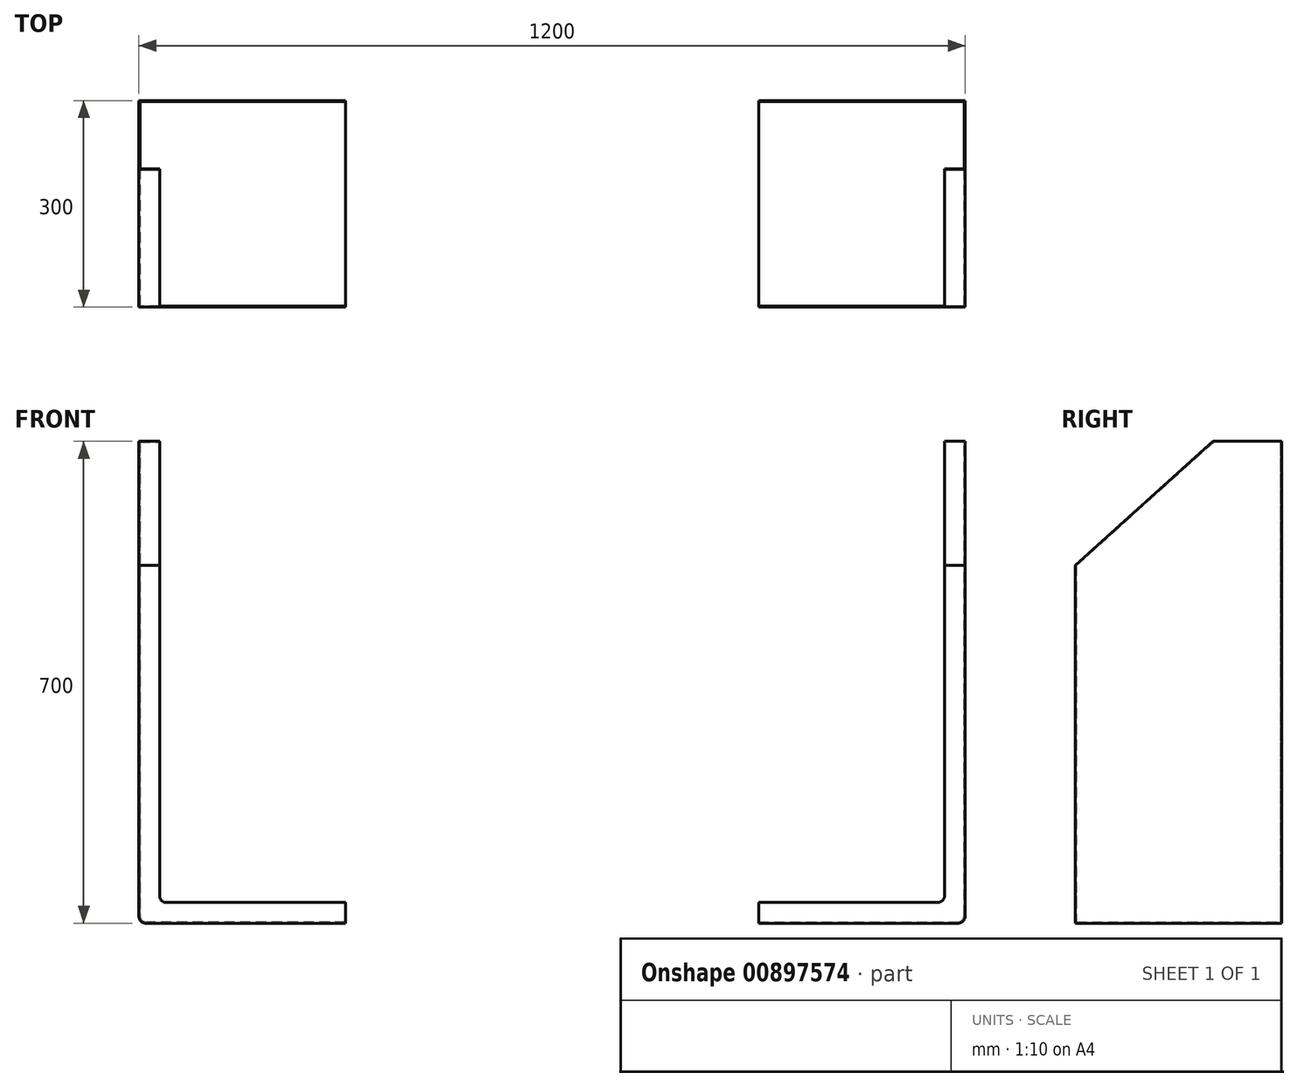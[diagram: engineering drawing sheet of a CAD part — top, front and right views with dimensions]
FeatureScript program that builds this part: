
annotation { "Feature Type Name" : "Feature", "Feature Type Description" : "" }
export const myFeature = defineFeature(function(context is Context, id is Id, definition is map)
    precondition{}
    {
        {
            var Q0;
            Q0=qCreatedBy(makeId("Front.planeOp"),FACE);
            var sketch = newSketch(context, id + "F0", { "sketchPlane" : qUnion([Q0])});
            skLineSegment(sketch, "E0.bottom", {"start": v(0, 0) * mm, "end": v(1.5, 0) * mm});
            skLineSegment(sketch, "E0.left", {"start": v(0, 0) * mm, "end": v(0, -690) * mm});
            skLineSegment(sketch, "E0.right", {"start": v(1.5, 0) * mm, "end": v(1.5, -688.5) * mm});
            skLineSegment(sketch, "E1.bottom", {"start": v(10, -700) * mm, "end": v(300, -700) * mm});
            skLineSegment(sketch, "E1.top", {"start": v(11.5, -698.5) * mm, "end": v(300, -698.5) * mm});
            skLineSegment(sketch, "E1.right", {"start": v(300, -700) * mm, "end": v(300, -698.5) * mm});
            skLineSegment(sketch, "E2", {"start": v(300, -700) * mm, "end": v(600, -700) * mm, "construction": true});
            skLineSegment(sketch, "E3", {"start": v(600, -700) * mm, "end": v(600, 159.83) * mm, "construction": true});
            skLineSegment(sketch, "E4.MirrorCS", {"start": v(1190, -700) * mm, "end": v(900, -700) * mm});
            skLineSegment(sketch, "E5.MirrorCS", {"start": v(1188.5, -698.5) * mm, "end": v(900, -698.5) * mm});
            skLineSegment(sketch, "E6.MirrorCS", {"start": v(900, -700) * mm, "end": v(900, -698.5) * mm});
            skLineSegment(sketch, "E7.MirrorCS", {"start": v(1200, 0) * mm, "end": v(1200, -690) * mm});
            skLineSegment(sketch, "E8.MirrorCS", {"start": v(1198.5, 0) * mm, "end": v(1198.5, -688.5) * mm});
            skLineSegment(sketch, "E9.MirrorCS", {"start": v(1200, 0) * mm, "end": v(1198.5, 0) * mm});
            skPoint(sketch, "E10.visualSharp", {"position": v(1.5, -698.5) * mm});
            skArc(sketch, "E10.filletArc", {"start": v(1.5, -688.5) * mm, "mid": v(4.43, -695.57) * mm, "end": v(11.5, -698.5) * mm});
            skPoint(sketch, "E11.visualSharp", {"position": v(0, -700) * mm});
            skArc(sketch, "E11.filletArc", {"start": v(0, -690) * mm, "mid": v(2.93, -697.07) * mm, "end": v(10, -700) * mm});
            skPoint(sketch, "E12.visualSharp", {"position": v(1198.5, -698.5) * mm});
            skArc(sketch, "E12.filletArc", {"start": v(1188.5, -698.5) * mm, "mid": v(1195.57, -695.57) * mm, "end": v(1198.5, -688.5) * mm});
            skPoint(sketch, "E13.visualSharp", {"position": v(1200, -700) * mm});
            skArc(sketch, "E13.filletArc", {"start": v(1190, -700) * mm, "mid": v(1197.07, -697.07) * mm, "end": v(1200, -690) * mm});
            skSolve(sketch);
        }
        {
            var Q0;
            Q0 = qSketchRegion(id + "F0", true);
            extrude(context, id + "F1", {"entities" : qUnion([Q0]), "depth" : 300 * mm, "offsetDistance" : 25 * mm});
        }
        {
            var Q0;
            Q0=makeQuery(id+"F1.opExtrude","CAP_EDGE",EDGE,{"disambiguationData":[OSD([sQuery(id+"F0.wireOp",EDGE,"E0.bottom")])],"isStart":false});
            chamfer(context, id + "F2", {"entities" : qUnion([Q0]), "chamferType" : ChamferType.TWO_OFFSETS, "width1" : 200 * mm, "oppositeDirection" : false, "width2" : 180 * mm});
        }
        {
            var Q0;
            Q0=makeQuery(id+"F1.opExtrude","CAP_FACE",FACE,{"disambiguationData":[OSD([sQuery(id+"F0.wireOp",EDGE,"E0.bottom"),sQuery(id+"F0.wireOp",EDGE,"E0.left"),sQuery(id+"F0.wireOp",EDGE,"E0.right"),sQuery(id+"F0.wireOp",EDGE,"E1.bottom"),sQuery(id+"F0.wireOp",EDGE,"E1.top"),sQuery(id+"F0.wireOp",EDGE,"E1.right")])],"isStart":false});
            var sketch = newSketch(context, id + "F3", { "sketchPlane" : qUnion([Q0])});
            skLineSegment(sketch, "E14.bottom", {"start": v(0, -180) * mm, "end": v(30, -180) * mm});
            skLineSegment(sketch, "E14.left", {"start": v(0, -180) * mm, "end": v(0, -690) * mm});
            skLineSegment(sketch, "E14.right", {"start": v(30, -180) * mm, "end": v(30, -660) * mm});
            skLineSegment(sketch, "E15.bottom", {"start": v(10, -700) * mm, "end": v(300, -700) * mm});
            skLineSegment(sketch, "E15.top", {"start": v(40, -670) * mm, "end": v(300, -670) * mm});
            skLineSegment(sketch, "E15.right", {"start": v(300, -700) * mm, "end": v(300, -670) * mm});
            skLineSegment(sketch, "E16.MirrorCS", {"start": v(900, -700) * mm, "end": v(900, -670) * mm});
            skLineSegment(sketch, "E17.MirrorCS", {"start": v(1160, -670) * mm, "end": v(900, -670) * mm});
            skLineSegment(sketch, "E18.MirrorCS", {"start": v(1190, -700) * mm, "end": v(900, -700) * mm});
            skLineSegment(sketch, "E19.MirrorCS", {"start": v(1170, -180) * mm, "end": v(1170, -660) * mm});
            skLineSegment(sketch, "E20.MirrorCS", {"start": v(1200, -180) * mm, "end": v(1200, -690) * mm});
            skLineSegment(sketch, "E21.MirrorCS", {"start": v(1200, -180) * mm, "end": v(1170, -180) * mm});
            skPoint(sketch, "E22.visualSharp", {"position": v(0, -700) * mm});
            skArc(sketch, "E22.filletArc", {"start": v(0, -690) * mm, "mid": v(2.93, -697.07) * mm, "end": v(10, -700) * mm});
            skPoint(sketch, "E23.visualSharp", {"position": v(30, -670) * mm});
            skArc(sketch, "E23.filletArc", {"start": v(30, -660) * mm, "mid": v(32.93, -667.07) * mm, "end": v(40, -670) * mm});
            skPoint(sketch, "E24.visualSharp", {"position": v(1170, -670) * mm});
            skArc(sketch, "E24.filletArc", {"start": v(1160, -670) * mm, "mid": v(1167.07, -667.07) * mm, "end": v(1170, -660) * mm});
            skPoint(sketch, "E25.visualSharp", {"position": v(1200, -700) * mm});
            skArc(sketch, "E25.filletArc", {"start": v(1190, -700) * mm, "mid": v(1197.07, -697.07) * mm, "end": v(1200, -690) * mm});
            skSolve(sketch);
        }
        {
            var Q0;
            Q0 = qSketchRegion(id + "F3", true);
            extrude(context, id + "F4", {"entities" : qUnion([Q0]), "operationType" : NewBodyOperationType.ADD, "oppositeDirection" : true, "depth" : 1.5 * mm, "offsetDistance" : 25 * mm});
        }
        {
            var Q0;
            Q0=makeQuery(id+"F2.opChamfer","BLEND_FACE",FACE,{"disambiguationData":[OSD([sQuery(id+"F0.wireOp",EDGE,"E0.bottom")])]});
            var sketch = newSketch(context, id + "F5", { "sketchPlane" : qUnion([Q0])});
            skLineSegment(sketch, "E26.bottom", {"start": v(0, -343.4) * mm, "end": v(30, -343.4) * mm});
            skLineSegment(sketch, "E26.top", {"start": v(0, -74.33) * mm, "end": v(30, -74.33) * mm});
            skLineSegment(sketch, "E26.left", {"start": v(0, -343.4) * mm, "end": v(0, -74.33) * mm});
            skLineSegment(sketch, "E26.right", {"start": v(30, -343.4) * mm, "end": v(30, -74.33) * mm});
            skLineSegment(sketch, "E27.MirrorCS", {"start": v(1170, -343.4) * mm, "end": v(1170, -74.33) * mm});
            skLineSegment(sketch, "E28.MirrorCS", {"start": v(1200, -343.4) * mm, "end": v(1170, -343.4) * mm});
            skLineSegment(sketch, "E29.MirrorCS", {"start": v(1200, -343.4) * mm, "end": v(1200, -74.33) * mm});
            skLineSegment(sketch, "E30.MirrorCS", {"start": v(1200, -74.33) * mm, "end": v(1170, -74.33) * mm});
            skSolve(sketch);
        }
        {
            var Q0;
            Q0 = qSketchRegion(id + "F5", true);
            extrude(context, id + "F6", {"entities" : qUnion([Q0]), "operationType" : NewBodyOperationType.ADD, "oppositeDirection" : true, "depth" : 1.5 * mm, "offsetDistance" : 25 * mm});
        }
        {
            var Q0;
            Q0=makeQuery(id+"F1.opExtrude","CAP_FACE",FACE,{"disambiguationData":[OSD([sQuery(id+"F0.wireOp",EDGE,"E0.bottom"),sQuery(id+"F0.wireOp",EDGE,"E0.left"),sQuery(id+"F0.wireOp",EDGE,"E0.right"),sQuery(id+"F0.wireOp",EDGE,"E1.bottom"),sQuery(id+"F0.wireOp",EDGE,"E1.top"),sQuery(id+"F0.wireOp",EDGE,"E1.right")])],"isStart":true});
            var sketch = newSketch(context, id + "F7", { "sketchPlane" : qUnion([Q0])});
            skLineSegment(sketch, "E31.bottom", {"start": v(-300, -700) * mm, "end": v(-10, -700) * mm});
            skLineSegment(sketch, "E31.top", {"start": v(-300, -670) * mm, "end": v(-40, -670) * mm});
            skLineSegment(sketch, "E31.left", {"start": v(-300, -700) * mm, "end": v(-300, -670) * mm});
            skLineSegment(sketch, "E32.top", {"start": v(0, 0) * mm, "end": v(-30, 0) * mm});
            skLineSegment(sketch, "E32.left", {"start": v(0, -690) * mm, "end": v(0, 0) * mm});
            skLineSegment(sketch, "E32.right", {"start": v(-30, -660) * mm, "end": v(-30, 0) * mm});
            skLineSegment(sketch, "E33.MirrorCS", {"start": v(-900, -700) * mm, "end": v(-1190, -700) * mm});
            skLineSegment(sketch, "E34.MirrorCS", {"start": v(-900, -700) * mm, "end": v(-900, -670) * mm});
            skLineSegment(sketch, "E35.MirrorCS", {"start": v(-900, -670) * mm, "end": v(-1160, -670) * mm});
            skLineSegment(sketch, "E36.MirrorCS", {"start": v(-1170, -660) * mm, "end": v(-1170, 0) * mm});
            skLineSegment(sketch, "E37.MirrorCS", {"start": v(-1200, -690) * mm, "end": v(-1200, 0) * mm});
            skLineSegment(sketch, "E38.MirrorCS", {"start": v(-1200, 0) * mm, "end": v(-1170, 0) * mm});
            skPoint(sketch, "E39.visualSharp", {"position": v(-1200, -700) * mm});
            skArc(sketch, "E39.filletArc", {"start": v(-1200, -690) * mm, "mid": v(-1197.07, -697.07) * mm, "end": v(-1190, -700) * mm});
            skPoint(sketch, "E40.visualSharp", {"position": v(-1170, -670) * mm});
            skArc(sketch, "E40.filletArc", {"start": v(-1170, -660) * mm, "mid": v(-1167.07, -667.07) * mm, "end": v(-1160, -670) * mm});
            skPoint(sketch, "E41.visualSharp", {"position": v(-30, -670) * mm});
            skArc(sketch, "E41.filletArc", {"start": v(-40, -670) * mm, "mid": v(-32.93, -667.07) * mm, "end": v(-30, -660) * mm});
            skPoint(sketch, "E42.visualSharp", {"position": v(0, -700) * mm});
            skArc(sketch, "E42.filletArc", {"start": v(-10, -700) * mm, "mid": v(-2.93, -697.07) * mm, "end": v(0, -690) * mm});
            skSolve(sketch);
        }
        {
            var Q0;
            Q0 = qSketchRegion(id + "F7", true);
            extrude(context, id + "F8", {"entities" : qUnion([Q0]), "operationType" : NewBodyOperationType.ADD, "oppositeDirection" : true, "depth" : 1.5 * mm, "offsetDistance" : 25 * mm});
        }
        {
            var Q0;
            Q0=makeQuery(id+"F1.opExtrude","CAP_EDGE",EDGE,{"disambiguationData":[OSD([sQuery(id+"F0.wireOp",EDGE,"E9.MirrorCS")])],"isStart":false});
            chamfer(context, id + "F9", {"entities" : qUnion([Q0]), "chamferType" : ChamferType.TWO_OFFSETS, "width1" : 180 * mm, "oppositeDirection" : false, "width2" : 200 * mm, "tangentPropagation" : true});
        }
    });
